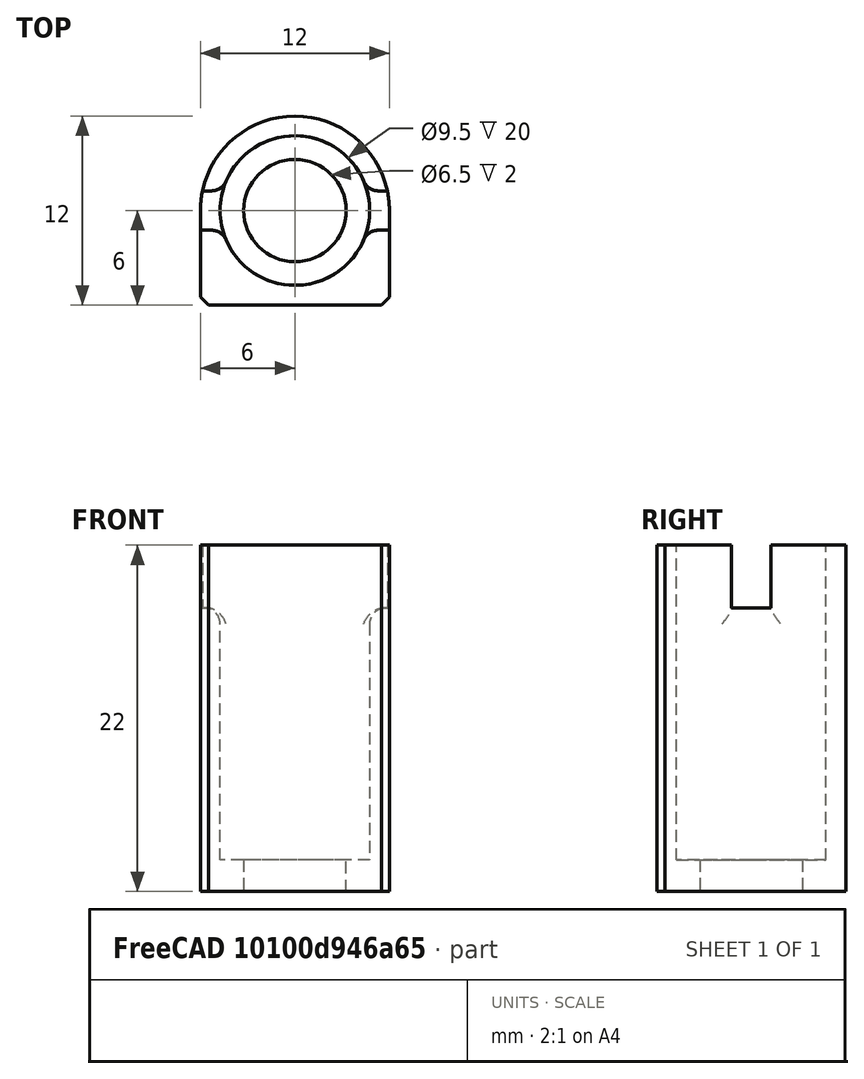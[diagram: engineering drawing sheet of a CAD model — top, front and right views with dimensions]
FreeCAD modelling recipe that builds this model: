
FCSTD DOCUMENT  (FreeCAD 0.17R13541 (Git))
Label: PiezoHub
License: All rights reserved
LicenseURL: http://en.wikipedia.org/wiki/All_rights_reserved
objects: Sketcher::SketchObject×4, PartDesign::Pocket×3, PartDesign::Pad×1, PartDesign::Fillet×1, PartDesign::Chamfer×1, PartDesign::Body×1, Mesh::Feature×1
note: 15 computed .brp shape members not serialized (recipe doc carries the construction recipe); baked Part::Feature solids carry a one-line shape summary decoded from their .brp

FEATURE [Sketcher::SketchObject] Sketch
  MapMode = 5
  Support = -> [XY_Plane]
  sketch-geometry (5):
    g0: Circle [constr] CenterX=0 CenterY=0 CenterZ=0 NormalX=0 NormalY=0 NormalZ=1 AngleXU=0 Radius=3
    g1: LineSegment StartX=-6 StartY=0 StartZ=0 EndX=-6 EndY=-6 EndZ=0
    g2: LineSegment StartX=-6 StartY=-6 StartZ=0 EndX=6 EndY=-6 EndZ=0
    g3: LineSegment StartX=6 StartY=-6 StartZ=0 EndX=6 EndY=0 EndZ=0
    g4: ArcOfCircle CenterX=0 CenterY=0 CenterZ=0 NormalX=0 NormalY=0 NormalZ=1 AngleXU=0 Radius=6 StartAngle=0 EndAngle=3.14159
  constraints (14):
    c: Coincident(g0,g-1)
    c: Radius(g0) = 3
    c: Vertical(g1)
    c: Coincident(g2,g1)
    c: Horizontal(g2)
    c: Coincident(g3,g2)
    c: Vertical(g3)
    c: Coincident(g4,g-1)
    c: Coincident(g1,g4)
    c: Coincident(g4,g3)
    c: PointOnObject(g1,g-1)
    c: PointOnObject(g3,g-1)
    c: Radius(g4) = 6
    c: DistanceY(g1,g-1) = 6
FEATURE [PartDesign::Pad] Pad
  Length = 22
  Length2 = 100
  Profile = -> Sketch
  Type = 0
FEATURE [Sketcher::SketchObject] Sketch001
  MapMode = 5
  Placement = pos=(0,0,0) rot=(1,0,0;3.14159rad)
  Support = -> [Pad]
  sketch-geometry (1):
    g0: Circle CenterX=0 CenterY=0 CenterZ=0 NormalX=0 NormalY=0 NormalZ=1 AngleXU=0 Radius=3.25
  constraints (2):
    c: Coincident(g0,g-1)
    c: Radius(g0) = 3.25
FEATURE [PartDesign::Pocket] Pocket
  BaseFeature = -> Pad
  Length = 5
  Length2 = 100
  Profile = -> Sketch001
  Type = 1
FEATURE [Sketcher::SketchObject] Sketch002
  MapMode = 5
  Placement = pos=(0,0,22) rot=(0,0,1;0rad)
  Support = -> [Pocket]
  sketch-geometry (1):
    g0: Circle CenterX=0 CenterY=0 CenterZ=0 NormalX=0 NormalY=0 NormalZ=1 AngleXU=0 Radius=4.75
  constraints (2):
    c: Coincident(g0,g-1)
    c: Radius(g0) = 4.75
FEATURE [PartDesign::Pocket] Pocket001
  BaseFeature = -> Pocket
  Length = 0
  Length2 = 100
  Offset = -2
  Profile = -> Sketch002
  Type = 3
  UpToFace = -> Pocket [Face4]
FEATURE [Sketcher::SketchObject] Sketch003
  ExternalGeometry = -> [Pocket001]
  MapMode = 5
  Placement = pos=(0,0,22) rot=(0,0,1;0rad)
  Support = -> [Pocket001]
  sketch-geometry (4):
    g0: LineSegment StartX=-6 StartY=1.25 StartZ=0 EndX=6 EndY=1.25 EndZ=0
    g1: LineSegment StartX=6 StartY=1.25 StartZ=0 EndX=6 EndY=-1.25 EndZ=0
    g2: LineSegment StartX=6 StartY=-1.25 StartZ=0 EndX=-6 EndY=-1.25 EndZ=0
    g3: LineSegment StartX=-6 StartY=-1.25 StartZ=0 EndX=-6 EndY=1.25 EndZ=0
  constraints (12):
    c: Coincident(g0,g1)
    c: Coincident(g1,g2)
    c: Coincident(g2,g3)
    c: Coincident(g3,g0)
    c: Horizontal(g0)
    c: Horizontal(g2)
    c: Vertical(g1)
    c: Vertical(g3)
    c: Symmetric(g0,g1,g-1)
    c: Symmetric(g0,g0,g-2)
    c: Distance(g1) = 2.5
    c: PointOnObject(g2,g-3)
FEATURE [PartDesign::Pocket] Pocket002
  BaseFeature = -> Pocket001
  Length = 4
  Length2 = 100
  Profile = -> Sketch003
  Type = 0
FEATURE [PartDesign::Fillet] Fillet
  Base = -> Pocket002 [Edge18,Edge20,Edge32,Edge33,Edge34,Edge37,Edge38]
  BaseFeature = -> Pocket002
  Radius = 1
FEATURE [PartDesign::Chamfer] Chamfer
  Base = -> Fillet [Edge28,Edge16]
  BaseFeature = -> Fillet
  Size = 0.5
FEATURE [PartDesign::Body] Body
  Group = -> [Sketch,Pad,Sketch001,Pocket,Sketch002,Pocket001,Sketch003,Pocket002,Fillet,Chamfer]
  Origin = -> Origin
  Tip = -> Chamfer
FEATURE [Mesh::Feature] Mesh  label="Chamfer (Meshed)"
